# Revit family: BE_99396_de_DE
name_source: partatom
category: Leuchten
units: mm (PartAtom-declared; Revit-internal decimal feet)

## family parameters
Basisbauteil = Fläche
Beim Laden mit Abzugskörper schneiden = Ja
Bemaßung runder Anschluss = Durchmesser verwenden
Gemeinsam genutzt = Nein
Lichtquelle = Ja
Raumberechnungspunkt = Ja
Teiletyp = Normal

## types (3) — shared parameters
AC/DC = DC
Aktualisierung = 2022-05-20T04:00:08
BEGA_Dummy = Nein
BEGA_IES = Ja
BEGA_Intern = Ja
BEGA_Intern_Konstruktion = Ja
BEGA_Intern_an = Ja
BEGA_Intern_aus = Ja
Befestigungsbohrung = Ø 70 mm
Beschreibung = Bodeneinbauleuchte
Beschreibung_Sonderanfertigung = Hier können Sie Informationen zur Sonderanfertigung eintragen.
Bestellnummer_Einbaugehäuse = ---
CE_Konformität = ja
Einbau_in_Wärmedämmung = ungeeignet
Einbaugehäuse = Nein
Einbautiefe = 100 mm
Einbauöffnung = 70 mm
Energieeffizienzklasse = LED A++ - A
Farbfilter = 16777215
Farbtemperaturverschiebung bei Dämpfen der Lampe = <Keine Auswahl>
Farbwiedergabeindex = CRI > 80
Gewicht = 0.8 kg
Hersteller = BEGA
Lampe = LED 3.4 W
Lastklassifizierung = Beleuchtung
Lebensdauerkriterien = L70B50 @ 25 °C = 200000 h
Logo = BEGA_Logo.png
Material_09 = BEGA_Glas_klar
Material_15 = BEGA_Leuchtmedium_matt
Material_17 = BEGA_Reflektor
Material_18 = BEGA_Gummi_schwarz
Neigungswinkel = 0.00°
Oberflächentemperatur = 35 °C
Produktdatenblatt = https://cdn.bega.com
Scheinlast = 0 VA
Schutzart = IP 68...20m
Schutzklasse = III
Sonderanfertigung = Nein
Spannung = 24 V
Typenbild = 99396.png
URL = https://www.bega.com
zero-valued in all types: Vorgabe-Ansicht

## per-type parameters (varying)
| type | Bestellnummer | Datei für fotometrisches Netz | Farbtemperatur | LED_Modulbezeichnung | Lampenlichtstrom | Leuchtenlichtstrom | Modell |
| BEGA_99396_K4 | 99396K4 | BE_99396K4.IES | 4000 K | LED-0386/840 | 500 lm | 272 lm | 99396K4 |
| BEGA_99396_K3 | 99396K3 | BE_99396K3.IES | 3000 K | LED-0386/830 | 495 lm | 271 lm | 99396K3 |
| BEGA_99396_K27 | 99396K27 | BE_99396K27.IES | 2700 K | LED-0386/827 | 490 lm | 268 lm | 99396K27 |
